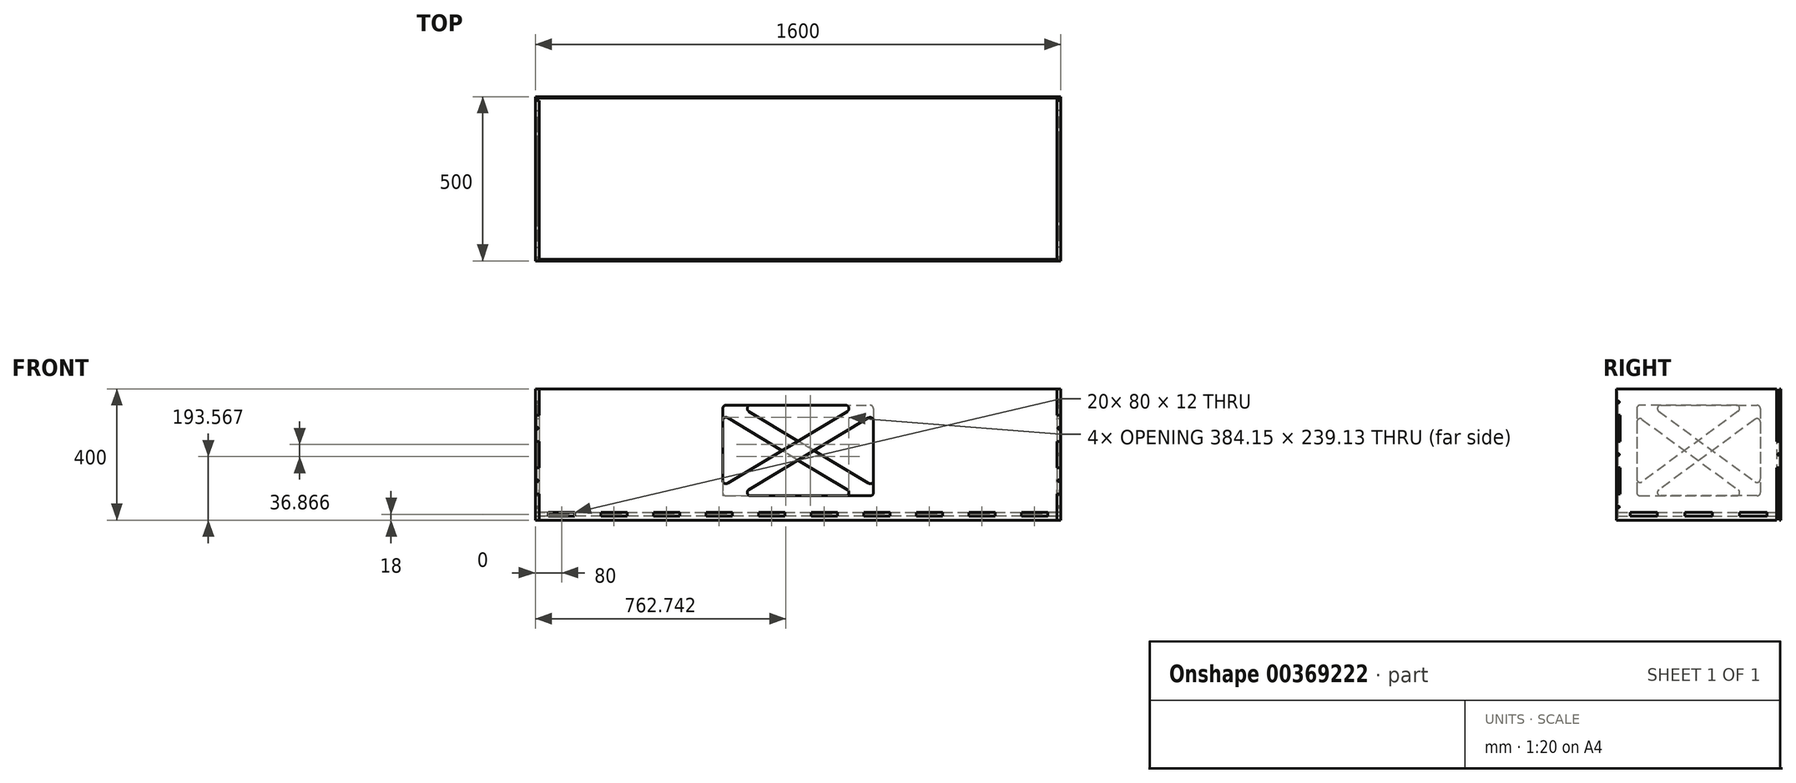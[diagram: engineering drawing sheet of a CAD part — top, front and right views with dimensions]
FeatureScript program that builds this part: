
annotation { "Feature Type Name" : "Feature", "Feature Type Description" : "" }
export const myFeature = defineFeature(function(context is Context, id is Id, definition is map)
    precondition{}
    {
        {
            assignVariable(context, id + "F0", {"name" : "lev", "anyValue" : 500});
        }
        {
            assignVariable(context, id + "F1", {"name" : "pit", "anyValue" : 1600});
        }
        {
            assignVariable(context, id + "F2", {"name" : "vaneri", "anyValue" : 12});
        }
        {
            assignVariable(context, id + "F3", {"name" : "ohut", "anyValue" : 4});
        }
        {
            var Q0;
            Q0=qCreatedBy(makeId("Right.planeOp"),FACE);
            var sketch = newSketch(context, id + "F4", { "sketchPlane" : qUnion([Q0])});
            skLineSegment(sketch, "E0.bottom", {"start": v(0, 0) * mm, "end": v(-500, 0) * mm});
            skLineSegment(sketch, "E0.top", {"start": v(0, 400) * mm, "end": v(-500, 400) * mm});
            skLineSegment(sketch, "E0.right", {"start": v(-500, 0) * mm, "end": v(-500, 80) * mm});
            skLineSegment(sketch, "E1.bottom", {"start": v(-500, 320) * mm, "end": v(-488, 320) * mm});
            skLineSegment(sketch, "E1.top", {"start": v(-500, 240) * mm, "end": v(-488, 240) * mm});
            skLineSegment(sketch, "E1.right", {"start": v(-488, 320) * mm, "end": v(-488, 240) * mm});
            skLineSegment(sketch, "E2.trimOffspring", {"start": v(-500, 320) * mm, "end": v(-500, 400) * mm});
            skCircle(sketch, "E3", {"center": v(-494, 360) * mm, "radius": 3 * mm});
            skPoint(sketch, "E3.centerSnap0", {"position": v(-500, 360) * mm});
            skPoint(sketch, "E3.centerSnap1", {"position": v(-494, 320) * mm});
            skLineSegment(sketch, "E4.bottom", {"start": v(-500, 160) * mm, "end": v(-488, 160) * mm});
            skLineSegment(sketch, "E4.top", {"start": v(-500, 80) * mm, "end": v(-488, 80) * mm});
            skLineSegment(sketch, "E4.right", {"start": v(-488, 160) * mm, "end": v(-488, 80) * mm});
            skLineSegment(sketch, "E5.trimOffspring", {"start": v(-500, 160) * mm, "end": v(-500, 240) * mm});
            skCircle(sketch, "E6", {"center": v(-494, 200) * mm, "radius": 3 * mm});
            skPoint(sketch, "E6.centerSnap0", {"position": v(-494, 240) * mm});
            skPoint(sketch, "E6.centerSnap1", {"position": v(-500, 200) * mm});
            skCircle(sketch, "E7", {"center": v(-494, 40) * mm, "radius": 3 * mm});
            skPoint(sketch, "E7.centerSnap0", {"position": v(-494, 80) * mm});
            skPoint(sketch, "E7.centerSnap1", {"position": v(-500, 40) * mm});
            skLineSegment(sketch, "E8", {"start": v(-250, 400) * mm, "end": v(-250, 0) * mm, "construction": true});
            skLineSegment(sketch, "E9.MirrorCS", {"start": v(0, 320) * mm, "end": v(0, 400) * mm});
            skLineSegment(sketch, "E10.MirrorCS", {"start": v(0, 0) * mm, "end": v(0, 80) * mm});
            skLineSegment(sketch, "E11.MirrorCS", {"start": v(0, 240) * mm, "end": v(-12, 240) * mm});
            skLineSegment(sketch, "E12.MirrorCS", {"start": v(0, 320) * mm, "end": v(-12, 320) * mm});
            skLineSegment(sketch, "E13.MirrorCS", {"start": v(0, 160) * mm, "end": v(-12, 160) * mm});
            skLineSegment(sketch, "E14.MirrorCS", {"start": v(0, 80) * mm, "end": v(-12, 80) * mm});
            skCircle(sketch, "E15.MirrorC", {"center": v(-6, 360) * mm, "radius": 3 * mm});
            skCircle(sketch, "E16.MirrorC", {"center": v(-6, 200) * mm, "radius": 3 * mm});
            skCircle(sketch, "E17.MirrorC", {"center": v(-6, 40) * mm, "radius": 3 * mm});
            skPoint(sketch, "E18.MirrorP", {"position": v(-6, 320) * mm});
            skLineSegment(sketch, "E19.MirrorCS", {"start": v(-12, 320) * mm, "end": v(-12, 240) * mm});
            skPoint(sketch, "E20.MirrorP", {"position": v(0, 40) * mm});
            skPoint(sketch, "E21.MirrorP", {"position": v(-6, 80) * mm});
            skPoint(sketch, "E22.MirrorP", {"position": v(0, 200) * mm});
            skLineSegment(sketch, "E23.MirrorCS", {"start": v(-12, 160) * mm, "end": v(-12, 80) * mm});
            skLineSegment(sketch, "E24.MirrorCS", {"start": v(0, 160) * mm, "end": v(0, 240) * mm});
            skPoint(sketch, "E25.MirrorP", {"position": v(0, 360) * mm});
            skPoint(sketch, "E26.MirrorP", {"position": v(-6, 240) * mm});
            skLineSegment(sketch, "E27.bottom", {"start": v(-458.33, 12) * mm, "end": v(-375, 12) * mm});
            skLineSegment(sketch, "E27.top", {"start": v(-458.33, 24) * mm, "end": v(-375, 24) * mm});
            skLineSegment(sketch, "E27.left", {"start": v(-458.33, 12) * mm, "end": v(-458.33, 24) * mm});
            skLineSegment(sketch, "E27.right", {"start": v(-375, 12) * mm, "end": v(-375, 24) * mm});
            skLineSegment(sketch, "E28.1.0.0", {"start": v(-208.33, 12) * mm, "end": v(-208.33, 24) * mm});
            skLineSegment(sketch, "E28.1.0.1", {"start": v(-291.67, 24) * mm, "end": v(-208.33, 24) * mm});
            skLineSegment(sketch, "E28.1.0.2", {"start": v(-291.67, 12) * mm, "end": v(-291.67, 24) * mm});
            skLineSegment(sketch, "E28.1.0.3", {"start": v(-291.67, 12) * mm, "end": v(-208.33, 12) * mm});
            skLineSegment(sketch, "E28.2.0.0", {"start": v(-41.67, 12) * mm, "end": v(-41.67, 24) * mm});
            skLineSegment(sketch, "E28.2.0.1", {"start": v(-125, 24) * mm, "end": v(-41.67, 24) * mm});
            skLineSegment(sketch, "E28.2.0.2", {"start": v(-125, 12) * mm, "end": v(-125, 24) * mm});
            skLineSegment(sketch, "E28.2.0.3", {"start": v(-125, 12) * mm, "end": v(-41.67, 12) * mm});
            skLineSegment(sketch, "E28.direction1", {"start": v(-458.33, 12) * mm, "end": v(-291.67, 12) * mm, "construction": true});
            skLineSegment(sketch, "E29.bottom", {"start": v(-365.23, 350) * mm, "end": v(-72, 350) * mm});
            skLineSegment(sketch, "E29.top", {"start": v(-428, 74) * mm, "end": v(-134.77, 74) * mm});
            skLineSegment(sketch, "E29.left", {"start": v(-438, 299.24) * mm, "end": v(-438, 84) * mm});
            skLineSegment(sketch, "E29.right", {"start": v(-62, 340) * mm, "end": v(-62, 124.76) * mm});
            skLineSegment(sketch, "E30", {"start": v(-438, 350) * mm, "end": v(-62, 74) * mm, "construction": true});
            skLineSegment(sketch, "E31", {"start": v(-371.15, 331.94) * mm, "end": v(-77.92, 116.7) * mm});
            skLineSegment(sketch, "E32", {"start": v(-422.08, 307.3) * mm, "end": v(-128.85, 92.06) * mm});
            skPoint(sketch, "E33.visualSharp", {"position": v(-438, 318.99) * mm});
            skArc(sketch, "E33.filletArc", {"start": v(-422.08, 307.3) * mm, "mid": v(-432.52, 308.16) * mm, "end": v(-438, 299.24) * mm});
            skPoint(sketch, "E34.visualSharp", {"position": v(-438, 74) * mm});
            skArc(sketch, "E34.filletArc", {"start": v(-438, 84) * mm, "mid": v(-435.07, 76.93) * mm, "end": v(-428, 74) * mm});
            skPoint(sketch, "E35.visualSharp", {"position": v(-104.25, 74) * mm});
            skArc(sketch, "E35.filletArc", {"start": v(-134.77, 74) * mm, "mid": v(-125.27, 80.89) * mm, "end": v(-128.85, 92.06) * mm});
            skPoint(sketch, "E36.visualSharp", {"position": v(-62, 105.01) * mm});
            skArc(sketch, "E36.filletArc", {"start": v(-77.92, 116.7) * mm, "mid": v(-67.48, 115.84) * mm, "end": v(-62, 124.76) * mm});
            skPoint(sketch, "E37.visualSharp", {"position": v(-395.75, 350) * mm});
            skArc(sketch, "E37.filletArc", {"start": v(-365.23, 350) * mm, "mid": v(-374.73, 343.11) * mm, "end": v(-371.15, 331.94) * mm});
            skPoint(sketch, "E38.visualSharp", {"position": v(-62, 350) * mm});
            skArc(sketch, "E38.filletArc", {"start": v(-62, 340) * mm, "mid": v(-64.93, 347.07) * mm, "end": v(-72, 350) * mm});
            skSolve(sketch);
        }
        {
            var Q0;
            Q0 = qSketchRegion(id + "F4", true);
            var Q1;
            Q1=makeQuery(id+"F4.imprint","IMPRINT",FACE,{"disambiguationData":[TD([[makeQuery(id+"F4.imprint","IMPRINT",EDGE,{"derivedFrom":sQuery(id+"F4.wireOp",EDGE,"E29.top")}),1.0]])]});
            var Q2;
            Q2=makeQuery(id+"F4.imprint","IMPRINT",FACE,{"disambiguationData":[TD([[makeQuery(id+"F4.imprint","IMPRINT",EDGE,{"derivedFrom":sQuery(id+"F4.wireOp",EDGE,"E29.bottom")}),-1.0]])]});
            extrude(context, id + "F5", {"entities" : qUnion([Q0, Q1, Q2]), "depth" : (getVariable(context, 'vaneri')) * mm});
        }
        {
            var Q0;
            Q0=makeQuery(id+"F4.imprint","IMPRINT",FACE,{"disambiguationData":[TD([[makeQuery(id+"F4.imprint","IMPRINT",EDGE,{"derivedFrom":sQuery(id+"F4.wireOp",EDGE,"E29.top")}),1.0]])]});
            var Q1;
            Q1=makeQuery(id+"F4.imprint","IMPRINT",FACE,{"disambiguationData":[TD([[makeQuery(id+"F4.imprint","IMPRINT",EDGE,{"derivedFrom":sQuery(id+"F4.wireOp",EDGE,"E29.bottom")}),-1.0]])]});
            extrude(context, id + "F6", {"entities" : qUnion([Q0, Q1]), "operationType" : NewBodyOperationType.REMOVE, "depth" : (getVariable(context, 'vaneri') - getVariable(context, 'ohut')) * mm});
        }
        {
            var Q0;
            Q0=makeQuery(id+"F5.opExtrude","SWEPT_BODY",BODY,{"disambiguationData":[OSD([sQuery(id+"F4.wireOp",EDGE,"E0.bottom"),sQuery(id+"F4.wireOp",EDGE,"E0.top"),sQuery(id+"F4.wireOp",EDGE,"E0.right"),sQuery(id+"F4.wireOp",EDGE,"E1.bottom"),sQuery(id+"F4.wireOp",EDGE,"E1.top"),sQuery(id+"F4.wireOp",EDGE,"E1.right"),sQuery(id+"F4.wireOp",EDGE,"E2.trimOffspring"),sQuery(id+"F4.wireOp",EDGE,"E3"),sQuery(id+"F4.wireOp",EDGE,"E4.bottom"),sQuery(id+"F4.wireOp",EDGE,"E4.top"),sQuery(id+"F4.wireOp",EDGE,"E4.right"),sQuery(id+"F4.wireOp",EDGE,"E5.trimOffspring"),sQuery(id+"F4.wireOp",EDGE,"E6"),sQuery(id+"F4.wireOp",EDGE,"E7"),sQuery(id+"F4.wireOp",EDGE,"E9.MirrorCS"),sQuery(id+"F4.wireOp",EDGE,"E10.MirrorCS"),sQuery(id+"F4.wireOp",EDGE,"E11.MirrorCS"),sQuery(id+"F4.wireOp",EDGE,"E12.MirrorCS"),sQuery(id+"F4.wireOp",EDGE,"E13.MirrorCS"),sQuery(id+"F4.wireOp",EDGE,"E14.MirrorCS"),sQuery(id+"F4.wireOp",EDGE,"E15.MirrorC"),sQuery(id+"F4.wireOp",EDGE,"E16.MirrorC"),sQuery(id+"F4.wireOp",EDGE,"E17.MirrorC"),sQuery(id+"F4.wireOp",EDGE,"E19.MirrorCS"),sQuery(id+"F4.wireOp",EDGE,"E23.MirrorCS"),sQuery(id+"F4.wireOp",EDGE,"E24.MirrorCS"),sQuery(id+"F4.wireOp",EDGE,"E27.bottom"),sQuery(id+"F4.wireOp",EDGE,"E27.top"),sQuery(id+"F4.wireOp",EDGE,"E27.left"),sQuery(id+"F4.wireOp",EDGE,"E27.right"),sQuery(id+"F4.wireOp",EDGE,"E28.1.0.0"),sQuery(id+"F4.wireOp",EDGE,"E28.1.0.1"),sQuery(id+"F4.wireOp",EDGE,"E28.1.0.2"),sQuery(id+"F4.wireOp",EDGE,"E28.1.0.3"),sQuery(id+"F4.wireOp",EDGE,"E28.2.0.0"),sQuery(id+"F4.wireOp",EDGE,"E28.2.0.1"),sQuery(id+"F4.wireOp",EDGE,"E28.2.0.2"),sQuery(id+"F4.wireOp",EDGE,"E28.2.0.3")])]});
            var Q1;
            Q1=sQuery(id+"F4.wireOp",EDGE,"E8");
            transform(context, id + "F7", {"entities" : qUnion([Q0]), "transformType" : TransformType.ROTATION, "transformAxis" : qUnion([Q1]), "angle" : 180 * degree, "makeCopy" : true});
        }
        {
            var Q0;
            Q0=makeQuery(id+"F7.opPattern","COPY",BODY,{"derivedFrom":makeQuery(id+"F5.opExtrude","SWEPT_BODY",BODY,{"disambiguationData":[OSD([sQuery(id+"F4.wireOp",EDGE,"E0.bottom"),sQuery(id+"F4.wireOp",EDGE,"E0.top"),sQuery(id+"F4.wireOp",EDGE,"E0.right"),sQuery(id+"F4.wireOp",EDGE,"E1.bottom"),sQuery(id+"F4.wireOp",EDGE,"E1.top"),sQuery(id+"F4.wireOp",EDGE,"E1.right"),sQuery(id+"F4.wireOp",EDGE,"E2.trimOffspring"),sQuery(id+"F4.wireOp",EDGE,"E3"),sQuery(id+"F4.wireOp",EDGE,"E4.bottom"),sQuery(id+"F4.wireOp",EDGE,"E4.top"),sQuery(id+"F4.wireOp",EDGE,"E4.right"),sQuery(id+"F4.wireOp",EDGE,"E5.trimOffspring"),sQuery(id+"F4.wireOp",EDGE,"E6"),sQuery(id+"F4.wireOp",EDGE,"E7"),sQuery(id+"F4.wireOp",EDGE,"E9.MirrorCS"),sQuery(id+"F4.wireOp",EDGE,"E10.MirrorCS"),sQuery(id+"F4.wireOp",EDGE,"E11.MirrorCS"),sQuery(id+"F4.wireOp",EDGE,"E12.MirrorCS"),sQuery(id+"F4.wireOp",EDGE,"E13.MirrorCS"),sQuery(id+"F4.wireOp",EDGE,"E14.MirrorCS"),sQuery(id+"F4.wireOp",EDGE,"E15.MirrorC"),sQuery(id+"F4.wireOp",EDGE,"E16.MirrorC"),sQuery(id+"F4.wireOp",EDGE,"E17.MirrorC"),sQuery(id+"F4.wireOp",EDGE,"E19.MirrorCS"),sQuery(id+"F4.wireOp",EDGE,"E23.MirrorCS"),sQuery(id+"F4.wireOp",EDGE,"E24.MirrorCS"),sQuery(id+"F4.wireOp",EDGE,"E27.bottom"),sQuery(id+"F4.wireOp",EDGE,"E27.top"),sQuery(id+"F4.wireOp",EDGE,"E27.left"),sQuery(id+"F4.wireOp",EDGE,"E27.right"),sQuery(id+"F4.wireOp",EDGE,"E28.1.0.0"),sQuery(id+"F4.wireOp",EDGE,"E28.1.0.1"),sQuery(id+"F4.wireOp",EDGE,"E28.1.0.2"),sQuery(id+"F4.wireOp",EDGE,"E28.1.0.3"),sQuery(id+"F4.wireOp",EDGE,"E28.2.0.0"),sQuery(id+"F4.wireOp",EDGE,"E28.2.0.1"),sQuery(id+"F4.wireOp",EDGE,"E28.2.0.2"),sQuery(id+"F4.wireOp",EDGE,"E28.2.0.3")])]}),"instanceName":"1"});
            transform(context, id + "F8", {"entities" : qUnion([Q0]), "transformType" : TransformType.TRANSLATION_3D, "dx" : (-(getVariable(context, 'pit') - 2 * getVariable(context, 'vaneri'))) * mm, "dy" : 0 * mm, "dz" : 0 * mm, "makeCopy" : false});
        }
        {
            var Q0;
            Q0=makeQuery(id+"F5.opExtrude","SWEPT_FACE",FACE,{"disambiguationData":[OSD([sQuery(id+"F4.wireOp",EDGE,"E24.MirrorCS")])]});
            var sketch = newSketch(context, id + "F9", { "sketchPlane" : qUnion([Q0])});
            skLineSegment(sketch, "E39.bottom", {"start": v(-12, 400) * mm, "end": v(1588, 400) * mm});
            skLineSegment(sketch, "E39.top", {"start": v(-12, 0) * mm, "end": v(1588, 0) * mm});
            skLineSegment(sketch, "E39.left", {"start": v(-12, 400) * mm, "end": v(-12, 0) * mm});
            skLineSegment(sketch, "E39.right", {"start": v(1588, 400) * mm, "end": v(1588, 0) * mm});
            skLineSegment(sketch, "E40.bottom", {"start": v(28, 12) * mm, "end": v(108, 12) * mm});
            skLineSegment(sketch, "E40.top", {"start": v(28, 24) * mm, "end": v(108, 24) * mm});
            skLineSegment(sketch, "E40.left", {"start": v(28, 12) * mm, "end": v(28, 24) * mm});
            skLineSegment(sketch, "E40.right", {"start": v(108, 12) * mm, "end": v(108, 24) * mm});
            skLineSegment(sketch, "E41.1.0.0", {"start": v(188, 24) * mm, "end": v(268, 24) * mm});
            skLineSegment(sketch, "E41.1.0.1", {"start": v(268, 12) * mm, "end": v(268, 24) * mm});
            skLineSegment(sketch, "E41.1.0.2", {"start": v(188, 12) * mm, "end": v(268, 12) * mm});
            skLineSegment(sketch, "E41.1.0.3", {"start": v(188, 12) * mm, "end": v(188, 24) * mm});
            skLineSegment(sketch, "E41.2.0.0", {"start": v(348, 24) * mm, "end": v(428, 24) * mm});
            skLineSegment(sketch, "E41.2.0.1", {"start": v(428, 12) * mm, "end": v(428, 24) * mm});
            skLineSegment(sketch, "E41.2.0.2", {"start": v(348, 12) * mm, "end": v(428, 12) * mm});
            skLineSegment(sketch, "E41.2.0.3", {"start": v(348, 12) * mm, "end": v(348, 24) * mm});
            skLineSegment(sketch, "E41.3.0.0", {"start": v(508, 24) * mm, "end": v(588, 24) * mm});
            skLineSegment(sketch, "E41.3.0.1", {"start": v(588, 12) * mm, "end": v(588, 24) * mm});
            skLineSegment(sketch, "E41.3.0.2", {"start": v(508, 12) * mm, "end": v(588, 12) * mm});
            skLineSegment(sketch, "E41.3.0.3", {"start": v(508, 12) * mm, "end": v(508, 24) * mm});
            skLineSegment(sketch, "E41.4.0.0", {"start": v(668, 24) * mm, "end": v(748, 24) * mm});
            skLineSegment(sketch, "E41.4.0.1", {"start": v(748, 12) * mm, "end": v(748, 24) * mm});
            skLineSegment(sketch, "E41.4.0.2", {"start": v(668, 12) * mm, "end": v(748, 12) * mm});
            skLineSegment(sketch, "E41.4.0.3", {"start": v(668, 12) * mm, "end": v(668, 24) * mm});
            skLineSegment(sketch, "E41.5.0.0", {"start": v(828, 24) * mm, "end": v(908, 24) * mm});
            skLineSegment(sketch, "E41.5.0.1", {"start": v(908, 12) * mm, "end": v(908, 24) * mm});
            skLineSegment(sketch, "E41.5.0.2", {"start": v(828, 12) * mm, "end": v(908, 12) * mm});
            skLineSegment(sketch, "E41.5.0.3", {"start": v(828, 12) * mm, "end": v(828, 24) * mm});
            skLineSegment(sketch, "E41.6.0.0", {"start": v(988, 24) * mm, "end": v(1068, 24) * mm});
            skLineSegment(sketch, "E41.6.0.1", {"start": v(1068, 12) * mm, "end": v(1068, 24) * mm});
            skLineSegment(sketch, "E41.6.0.2", {"start": v(988, 12) * mm, "end": v(1068, 12) * mm});
            skLineSegment(sketch, "E41.6.0.3", {"start": v(988, 12) * mm, "end": v(988, 24) * mm});
            skLineSegment(sketch, "E41.7.0.0", {"start": v(1148, 24) * mm, "end": v(1228, 24) * mm});
            skLineSegment(sketch, "E41.7.0.1", {"start": v(1228, 12) * mm, "end": v(1228, 24) * mm});
            skLineSegment(sketch, "E41.7.0.2", {"start": v(1148, 12) * mm, "end": v(1228, 12) * mm});
            skLineSegment(sketch, "E41.7.0.3", {"start": v(1148, 12) * mm, "end": v(1148, 24) * mm});
            skLineSegment(sketch, "E41.8.0.0", {"start": v(1308, 24) * mm, "end": v(1388, 24) * mm});
            skLineSegment(sketch, "E41.8.0.1", {"start": v(1388, 12) * mm, "end": v(1388, 24) * mm});
            skLineSegment(sketch, "E41.8.0.2", {"start": v(1308, 12) * mm, "end": v(1388, 12) * mm});
            skLineSegment(sketch, "E41.8.0.3", {"start": v(1308, 12) * mm, "end": v(1308, 24) * mm});
            skLineSegment(sketch, "E41.9.0.0", {"start": v(1468, 24) * mm, "end": v(1548, 24) * mm});
            skLineSegment(sketch, "E41.9.0.1", {"start": v(1548, 12) * mm, "end": v(1548, 24) * mm});
            skLineSegment(sketch, "E41.9.0.2", {"start": v(1468, 12) * mm, "end": v(1548, 12) * mm});
            skLineSegment(sketch, "E41.9.0.3", {"start": v(1468, 12) * mm, "end": v(1468, 24) * mm});
            skLineSegment(sketch, "E41.direction1", {"start": v(28, 12) * mm, "end": v(188, 12) * mm, "construction": true});
            skLineSegment(sketch, "E42", {"start": v(50, 303.13) * mm, "end": v(50, 84) * mm});
            skLineSegment(sketch, "E43", {"start": v(60, 74) * mm, "end": v(424.17, 74) * mm});
            skLineSegment(sketch, "E44", {"start": v(429.32, 92.57) * mm, "end": v(65.16, 311.7) * mm});
            skLineSegment(sketch, "E45", {"start": v(134.5, 350) * mm, "end": v(498.67, 350) * mm});
            skLineSegment(sketch, "E46", {"start": v(508.67, 340) * mm, "end": v(508.67, 120.87) * mm});
            skLineSegment(sketch, "E47", {"start": v(493.51, 112.3) * mm, "end": v(129.35, 331.43) * mm});
            skLineSegment(sketch, "E48", {"start": v(508.67, 103.18) * mm, "end": v(508.67, 74) * mm, "construction": true});
            skLineSegment(sketch, "E49", {"start": v(508.67, 74) * mm, "end": v(460.18, 74) * mm, "construction": true});
            skLineSegment(sketch, "E50", {"start": v(50, 320.82) * mm, "end": v(50, 350) * mm, "construction": true});
            skLineSegment(sketch, "E51", {"start": v(50, 350) * mm, "end": v(98.49, 350) * mm, "construction": true});
            skLineSegment(sketch, "E52", {"start": v(50, 350) * mm, "end": v(508.67, 74) * mm, "construction": true});
            skLineSegment(sketch, "E53", {"start": v(533.67, 400) * mm, "end": v(533.67, 0) * mm, "construction": true});
            skArc(sketch, "E54", {"start": v(50, 84) * mm, "mid": v(52.93, 76.93) * mm, "end": v(60, 74) * mm});
            skArc(sketch, "E55", {"start": v(65.16, 311.7) * mm, "mid": v(55.08, 311.84) * mm, "end": v(50, 303.13) * mm});
            skArc(sketch, "E56", {"start": v(424.17, 74) * mm, "mid": v(433.8, 81.32) * mm, "end": v(429.32, 92.57) * mm});
            skArc(sketch, "E57", {"start": v(134.5, 350) * mm, "mid": v(124.87, 342.68) * mm, "end": v(129.35, 331.43) * mm});
            skArc(sketch, "E58", {"start": v(508.67, 340) * mm, "mid": v(505.74, 347.07) * mm, "end": v(498.67, 350) * mm});
            skArc(sketch, "E59", {"start": v(493.51, 112.3) * mm, "mid": v(503.59, 112.16) * mm, "end": v(508.67, 120.87) * mm});
            skArc(sketch, "E60.MirrorCS", {"start": v(573.82, 112.3) * mm, "mid": v(563.75, 112.16) * mm, "end": v(558.67, 120.87) * mm});
            skArc(sketch, "E61.MirrorCS", {"start": v(932.83, 350) * mm, "mid": v(942.47, 342.68) * mm, "end": v(937.99, 331.43) * mm});
            skArc(sketch, "E62.MirrorCS", {"start": v(558.67, 340) * mm, "mid": v(561.6, 347.07) * mm, "end": v(568.67, 350) * mm});
            skArc(sketch, "E63.MirrorCS", {"start": v(1017.33, 84) * mm, "mid": v(1014.4, 76.93) * mm, "end": v(1007.33, 74) * mm});
            skArc(sketch, "E64.MirrorCS", {"start": v(1002.18, 311.7) * mm, "mid": v(1012.25, 311.84) * mm, "end": v(1017.33, 303.13) * mm});
            skLineSegment(sketch, "E65.MirrorCS", {"start": v(1017.33, 350) * mm, "end": v(558.67, 74) * mm, "construction": true});
            skLineSegment(sketch, "E66.MirrorCS", {"start": v(932.83, 350) * mm, "end": v(568.67, 350) * mm});
            skLineSegment(sketch, "E67.MirrorCS", {"start": v(1017.33, 320.82) * mm, "end": v(1017.33, 350) * mm, "construction": true});
            skLineSegment(sketch, "E68.MirrorCS", {"start": v(638.01, 92.57) * mm, "end": v(1002.18, 311.7) * mm});
            skLineSegment(sketch, "E69.MirrorCS", {"start": v(1017.33, 350) * mm, "end": v(968.85, 350) * mm, "construction": true});
            skArc(sketch, "E70.MirrorCS", {"start": v(643.17, 74) * mm, "mid": v(633.53, 81.32) * mm, "end": v(638.01, 92.57) * mm});
            skLineSegment(sketch, "E71.MirrorCS", {"start": v(1007.33, 74) * mm, "end": v(643.17, 74) * mm});
            skLineSegment(sketch, "E72.MirrorCS", {"start": v(558.67, 74) * mm, "end": v(607.15, 74) * mm, "construction": true});
            skLineSegment(sketch, "E73.MirrorCS", {"start": v(558.67, 103.18) * mm, "end": v(558.67, 74) * mm, "construction": true});
            skLineSegment(sketch, "E74.MirrorCS", {"start": v(1017.33, 303.13) * mm, "end": v(1017.33, 84) * mm});
            skLineSegment(sketch, "E75.MirrorCS", {"start": v(558.67, 340) * mm, "end": v(558.67, 120.87) * mm});
            skLineSegment(sketch, "E76.MirrorCS", {"start": v(573.82, 112.3) * mm, "end": v(937.99, 331.43) * mm});
            skLineSegment(sketch, "E77", {"start": v(1042.33, 400) * mm, "end": v(1042.33, 0) * mm, "construction": true});
            skArc(sketch, "E78.MirrorCS", {"start": v(1151.83, 350) * mm, "mid": v(1142.2, 342.68) * mm, "end": v(1146.68, 331.43) * mm});
            skArc(sketch, "E79.MirrorCS", {"start": v(1082.49, 311.7) * mm, "mid": v(1072.41, 311.84) * mm, "end": v(1067.33, 303.13) * mm});
            skArc(sketch, "E80.MirrorCS", {"start": v(1526, 340) * mm, "mid": v(1523.07, 347.07) * mm, "end": v(1516, 350) * mm});
            skArc(sketch, "E81.MirrorCS", {"start": v(1441.5, 74) * mm, "mid": v(1451.13, 81.32) * mm, "end": v(1446.65, 92.57) * mm});
            skArc(sketch, "E82.MirrorCS", {"start": v(1510.84, 112.3) * mm, "mid": v(1520.92, 112.16) * mm, "end": v(1526, 120.87) * mm});
            skArc(sketch, "E83.MirrorCS", {"start": v(1067.33, 84) * mm, "mid": v(1070.26, 76.93) * mm, "end": v(1077.33, 74) * mm});
            skLineSegment(sketch, "E84.MirrorCS", {"start": v(1526, 103.18) * mm, "end": v(1526, 74) * mm, "construction": true});
            skLineSegment(sketch, "E85.MirrorCS", {"start": v(1151.83, 350) * mm, "end": v(1516, 350) * mm});
            skLineSegment(sketch, "E86.MirrorCS", {"start": v(1077.33, 74) * mm, "end": v(1441.5, 74) * mm});
            skLineSegment(sketch, "E87.MirrorCS", {"start": v(1446.65, 92.57) * mm, "end": v(1082.49, 311.7) * mm});
            skLineSegment(sketch, "E88.MirrorCS", {"start": v(1526, 340) * mm, "end": v(1526, 120.87) * mm});
            skLineSegment(sketch, "E89.MirrorCS", {"start": v(1510.84, 112.3) * mm, "end": v(1146.68, 331.43) * mm});
            skLineSegment(sketch, "E90.MirrorCS", {"start": v(1067.33, 320.82) * mm, "end": v(1067.33, 350) * mm, "construction": true});
            skLineSegment(sketch, "E91.MirrorCS", {"start": v(1526, 74) * mm, "end": v(1477.51, 74) * mm, "construction": true});
            skLineSegment(sketch, "E92.MirrorCS", {"start": v(1067.33, 350) * mm, "end": v(1115.82, 350) * mm, "construction": true});
            skLineSegment(sketch, "E93.MirrorCS", {"start": v(1067.33, 350) * mm, "end": v(1526, 74) * mm, "construction": true});
            skLineSegment(sketch, "E94.MirrorCS", {"start": v(1067.33, 303.13) * mm, "end": v(1067.33, 84) * mm});
            skCircle(sketch, "E95", {"center": v(-6, 280) * mm, "radius": 3 * mm});
            skCircle(sketch, "E96", {"center": v(-6, 120) * mm, "radius": 3 * mm});
            skLineSegment(sketch, "E97", {"start": v(-12, 280) * mm, "end": v(0, 280) * mm, "construction": true});
            skLineSegment(sketch, "E98", {"start": v(-12, 120) * mm, "end": v(0, 120) * mm, "construction": true});
            skLineSegment(sketch, "E99", {"start": v(788, 400) * mm, "end": v(788, 0) * mm, "construction": true});
            skCircle(sketch, "E100.MirrorC", {"center": v(1582, 280) * mm, "radius": 3 * mm});
            skCircle(sketch, "E101.MirrorC", {"center": v(1582, 120) * mm, "radius": 3 * mm});
            skLineSegment(sketch, "E102.MirrorCS", {"start": v(1588, 280) * mm, "end": v(1576, 280) * mm, "construction": true});
            skLineSegment(sketch, "E103.MirrorCS", {"start": v(1588, 120) * mm, "end": v(1576, 120) * mm, "construction": true});
            skSolve(sketch);
        }
        {
            var Q0;
            Q0 = qSketchRegion(id + "F9", true);
            var Q1;
            Q1=makeQuery(id+"F9.imprint","IMPRINT",FACE,{"disambiguationData":[TD([[makeQuery(id+"F9.imprint","IMPRINT",EDGE,{"derivedFrom":sQuery(id+"F9.wireOp",EDGE,"E42")}),1.0]])]});
            var Q2;
            Q2=makeQuery(id+"F9.imprint","IMPRINT",FACE,{"disambiguationData":[TD([[makeQuery(id+"F9.imprint","IMPRINT",EDGE,{"derivedFrom":sQuery(id+"F9.wireOp",EDGE,"E45")}),-1.0]])]});
            var Q3;
            Q3=makeQuery(id+"F9.imprint","IMPRINT",FACE,{"disambiguationData":[TD([[makeQuery(id+"F9.imprint","IMPRINT",EDGE,{"derivedFrom":sQuery(id+"F9.wireOp",EDGE,"E60.MirrorCS")}),-1.0]])]});
            var Q4;
            Q4=makeQuery(id+"F9.imprint","IMPRINT",FACE,{"disambiguationData":[TD([[makeQuery(id+"F9.imprint","IMPRINT",EDGE,{"derivedFrom":sQuery(id+"F9.wireOp",EDGE,"E63.MirrorCS")}),-1.0]])]});
            var Q5;
            Q5=makeQuery(id+"F9.imprint","IMPRINT",FACE,{"disambiguationData":[TD([[makeQuery(id+"F9.imprint","IMPRINT",EDGE,{"derivedFrom":sQuery(id+"F9.wireOp",EDGE,"E79.MirrorCS")}),1.0]])]});
            var Q6;
            Q6=makeQuery(id+"F9.imprint","IMPRINT",FACE,{"disambiguationData":[TD([[makeQuery(id+"F9.imprint","IMPRINT",EDGE,{"derivedFrom":sQuery(id+"F9.wireOp",EDGE,"E78.MirrorCS")}),1.0]])]});
            extrude(context, id + "F10", {"entities" : qUnion([Q0, Q1, Q2, Q3, Q4, Q5, Q6]), "oppositeDirection" : true, "depth" : (getVariable(context, 'vaneri')) * mm});
        }
        {
            var Q0;
            Q0=makeQuery(id+"F9.imprint","IMPRINT",FACE,{"disambiguationData":[TD([[makeQuery(id+"F9.imprint","IMPRINT",EDGE,{"derivedFrom":sQuery(id+"F9.wireOp",EDGE,"E42")}),1.0]])]});
            var Q1;
            Q1=makeQuery(id+"F9.imprint","IMPRINT",FACE,{"disambiguationData":[TD([[makeQuery(id+"F9.imprint","IMPRINT",EDGE,{"derivedFrom":sQuery(id+"F9.wireOp",EDGE,"E45")}),-1.0]])]});
            var Q2;
            Q2=makeQuery(id+"F9.imprint","IMPRINT",FACE,{"disambiguationData":[TD([[makeQuery(id+"F9.imprint","IMPRINT",EDGE,{"derivedFrom":sQuery(id+"F9.wireOp",EDGE,"E60.MirrorCS")}),-1.0]])]});
            var Q3;
            Q3=makeQuery(id+"F9.imprint","IMPRINT",FACE,{"disambiguationData":[TD([[makeQuery(id+"F9.imprint","IMPRINT",EDGE,{"derivedFrom":sQuery(id+"F9.wireOp",EDGE,"E63.MirrorCS")}),-1.0]])]});
            var Q4;
            Q4=makeQuery(id+"F9.imprint","IMPRINT",FACE,{"disambiguationData":[TD([[makeQuery(id+"F9.imprint","IMPRINT",EDGE,{"derivedFrom":sQuery(id+"F9.wireOp",EDGE,"E79.MirrorCS")}),1.0]])]});
            var Q5;
            Q5=makeQuery(id+"F9.imprint","IMPRINT",FACE,{"disambiguationData":[TD([[makeQuery(id+"F9.imprint","IMPRINT",EDGE,{"derivedFrom":sQuery(id+"F9.wireOp",EDGE,"E78.MirrorCS")}),1.0]])]});
            extrude(context, id + "F11", {"entities" : qUnion([Q0, Q1, Q2, Q3, Q4, Q5]), "operationType" : NewBodyOperationType.REMOVE, "oppositeDirection" : true, "depth" : (getVariable(context, 'vaneri')) * mm, "hasSecondDirection" : true, "secondDirectionOppositeDirection" : true, "secondDirectionDepth" : (getVariable(context, 'ohut')) * mm});
        }
        {
            var Q0;
            Q0=makeQuery(id+"F5.opExtrude","SWEPT_BODY",BODY,{"disambiguationData":[OSD([sQuery(id+"F4.wireOp",EDGE,"E0.bottom"),sQuery(id+"F4.wireOp",EDGE,"E0.top"),sQuery(id+"F4.wireOp",EDGE,"E0.right"),sQuery(id+"F4.wireOp",EDGE,"E1.bottom"),sQuery(id+"F4.wireOp",EDGE,"E1.top"),sQuery(id+"F4.wireOp",EDGE,"E1.right"),sQuery(id+"F4.wireOp",EDGE,"E2.trimOffspring"),sQuery(id+"F4.wireOp",EDGE,"E3"),sQuery(id+"F4.wireOp",EDGE,"E4.bottom"),sQuery(id+"F4.wireOp",EDGE,"E4.top"),sQuery(id+"F4.wireOp",EDGE,"E4.right"),sQuery(id+"F4.wireOp",EDGE,"E5.trimOffspring"),sQuery(id+"F4.wireOp",EDGE,"E6"),sQuery(id+"F4.wireOp",EDGE,"E7"),sQuery(id+"F4.wireOp",EDGE,"E9.MirrorCS"),sQuery(id+"F4.wireOp",EDGE,"E10.MirrorCS"),sQuery(id+"F4.wireOp",EDGE,"E11.MirrorCS"),sQuery(id+"F4.wireOp",EDGE,"E12.MirrorCS"),sQuery(id+"F4.wireOp",EDGE,"E13.MirrorCS"),sQuery(id+"F4.wireOp",EDGE,"E14.MirrorCS"),sQuery(id+"F4.wireOp",EDGE,"E15.MirrorC"),sQuery(id+"F4.wireOp",EDGE,"E16.MirrorC"),sQuery(id+"F4.wireOp",EDGE,"E17.MirrorC"),sQuery(id+"F4.wireOp",EDGE,"E19.MirrorCS"),sQuery(id+"F4.wireOp",EDGE,"E23.MirrorCS"),sQuery(id+"F4.wireOp",EDGE,"E24.MirrorCS"),sQuery(id+"F4.wireOp",EDGE,"E27.bottom"),sQuery(id+"F4.wireOp",EDGE,"E27.top"),sQuery(id+"F4.wireOp",EDGE,"E27.left"),sQuery(id+"F4.wireOp",EDGE,"E27.right"),sQuery(id+"F4.wireOp",EDGE,"E28.1.0.0"),sQuery(id+"F4.wireOp",EDGE,"E28.1.0.1"),sQuery(id+"F4.wireOp",EDGE,"E28.1.0.2"),sQuery(id+"F4.wireOp",EDGE,"E28.1.0.3"),sQuery(id+"F4.wireOp",EDGE,"E28.2.0.0"),sQuery(id+"F4.wireOp",EDGE,"E28.2.0.1"),sQuery(id+"F4.wireOp",EDGE,"E28.2.0.2"),sQuery(id+"F4.wireOp",EDGE,"E28.2.0.3")])]});
            var Q1;
            Q1=makeQuery(id+"F7.opPattern","COPY",BODY,{"derivedFrom":makeQuery(id+"F5.opExtrude","SWEPT_BODY",BODY,{"disambiguationData":[OSD([sQuery(id+"F4.wireOp",EDGE,"E0.bottom"),sQuery(id+"F4.wireOp",EDGE,"E0.top"),sQuery(id+"F4.wireOp",EDGE,"E0.right"),sQuery(id+"F4.wireOp",EDGE,"E1.bottom"),sQuery(id+"F4.wireOp",EDGE,"E1.top"),sQuery(id+"F4.wireOp",EDGE,"E1.right"),sQuery(id+"F4.wireOp",EDGE,"E2.trimOffspring"),sQuery(id+"F4.wireOp",EDGE,"E3"),sQuery(id+"F4.wireOp",EDGE,"E4.bottom"),sQuery(id+"F4.wireOp",EDGE,"E4.top"),sQuery(id+"F4.wireOp",EDGE,"E4.right"),sQuery(id+"F4.wireOp",EDGE,"E5.trimOffspring"),sQuery(id+"F4.wireOp",EDGE,"E6"),sQuery(id+"F4.wireOp",EDGE,"E7"),sQuery(id+"F4.wireOp",EDGE,"E9.MirrorCS"),sQuery(id+"F4.wireOp",EDGE,"E10.MirrorCS"),sQuery(id+"F4.wireOp",EDGE,"E11.MirrorCS"),sQuery(id+"F4.wireOp",EDGE,"E12.MirrorCS"),sQuery(id+"F4.wireOp",EDGE,"E13.MirrorCS"),sQuery(id+"F4.wireOp",EDGE,"E14.MirrorCS"),sQuery(id+"F4.wireOp",EDGE,"E15.MirrorC"),sQuery(id+"F4.wireOp",EDGE,"E16.MirrorC"),sQuery(id+"F4.wireOp",EDGE,"E17.MirrorC"),sQuery(id+"F4.wireOp",EDGE,"E19.MirrorCS"),sQuery(id+"F4.wireOp",EDGE,"E23.MirrorCS"),sQuery(id+"F4.wireOp",EDGE,"E24.MirrorCS"),sQuery(id+"F4.wireOp",EDGE,"E27.bottom"),sQuery(id+"F4.wireOp",EDGE,"E27.top"),sQuery(id+"F4.wireOp",EDGE,"E27.left"),sQuery(id+"F4.wireOp",EDGE,"E27.right"),sQuery(id+"F4.wireOp",EDGE,"E28.1.0.0"),sQuery(id+"F4.wireOp",EDGE,"E28.1.0.1"),sQuery(id+"F4.wireOp",EDGE,"E28.1.0.2"),sQuery(id+"F4.wireOp",EDGE,"E28.1.0.3"),sQuery(id+"F4.wireOp",EDGE,"E28.2.0.0"),sQuery(id+"F4.wireOp",EDGE,"E28.2.0.1"),sQuery(id+"F4.wireOp",EDGE,"E28.2.0.2"),sQuery(id+"F4.wireOp",EDGE,"E28.2.0.3")])]}),"instanceName":"1"});
            var Q2;
            Q2=makeQuery(id+"F10.opExtrude","SWEPT_BODY",BODY,{"disambiguationData":[OSD([sQuery(id+"F9.wireOp",EDGE,"E39.bottom"),sQuery(id+"F9.wireOp",EDGE,"E39.top"),sQuery(id+"F9.wireOp",EDGE,"E39.left"),sQuery(id+"F9.wireOp",EDGE,"E39.right"),sQuery(id+"F9.wireOp",EDGE,"E40.bottom"),sQuery(id+"F9.wireOp",EDGE,"E40.top"),sQuery(id+"F9.wireOp",EDGE,"E40.left"),sQuery(id+"F9.wireOp",EDGE,"E40.right"),sQuery(id+"F9.wireOp",EDGE,"E41.1.0.0"),sQuery(id+"F9.wireOp",EDGE,"E41.1.0.1"),sQuery(id+"F9.wireOp",EDGE,"E41.1.0.2"),sQuery(id+"F9.wireOp",EDGE,"E41.1.0.3"),sQuery(id+"F9.wireOp",EDGE,"E41.2.0.0"),sQuery(id+"F9.wireOp",EDGE,"E41.2.0.1"),sQuery(id+"F9.wireOp",EDGE,"E41.2.0.2"),sQuery(id+"F9.wireOp",EDGE,"E41.2.0.3"),sQuery(id+"F9.wireOp",EDGE,"E41.3.0.0"),sQuery(id+"F9.wireOp",EDGE,"E41.3.0.1"),sQuery(id+"F9.wireOp",EDGE,"E41.3.0.2"),sQuery(id+"F9.wireOp",EDGE,"E41.3.0.3"),sQuery(id+"F9.wireOp",EDGE,"E41.4.0.0"),sQuery(id+"F9.wireOp",EDGE,"E41.4.0.1"),sQuery(id+"F9.wireOp",EDGE,"E41.4.0.2"),sQuery(id+"F9.wireOp",EDGE,"E41.4.0.3"),sQuery(id+"F9.wireOp",EDGE,"E41.5.0.0"),sQuery(id+"F9.wireOp",EDGE,"E41.5.0.1"),sQuery(id+"F9.wireOp",EDGE,"E41.5.0.2"),sQuery(id+"F9.wireOp",EDGE,"E41.5.0.3"),sQuery(id+"F9.wireOp",EDGE,"E41.6.0.0"),sQuery(id+"F9.wireOp",EDGE,"E41.6.0.1"),sQuery(id+"F9.wireOp",EDGE,"E41.6.0.2"),sQuery(id+"F9.wireOp",EDGE,"E41.6.0.3"),sQuery(id+"F9.wireOp",EDGE,"E41.7.0.0"),sQuery(id+"F9.wireOp",EDGE,"E41.7.0.1"),sQuery(id+"F9.wireOp",EDGE,"E41.7.0.2"),sQuery(id+"F9.wireOp",EDGE,"E41.7.0.3"),sQuery(id+"F9.wireOp",EDGE,"E41.8.0.0"),sQuery(id+"F9.wireOp",EDGE,"E41.8.0.1"),sQuery(id+"F9.wireOp",EDGE,"E41.8.0.2"),sQuery(id+"F9.wireOp",EDGE,"E41.8.0.3"),sQuery(id+"F9.wireOp",EDGE,"E41.9.0.0"),sQuery(id+"F9.wireOp",EDGE,"E41.9.0.1"),sQuery(id+"F9.wireOp",EDGE,"E41.9.0.2"),sQuery(id+"F9.wireOp",EDGE,"E41.9.0.3"),sQuery(id+"F9.wireOp",EDGE,"E95"),sQuery(id+"F9.wireOp",EDGE,"E96"),sQuery(id+"F9.wireOp",EDGE,"E100.MirrorC"),sQuery(id+"F9.wireOp",EDGE,"E101.MirrorC")])]});
            booleanBodies(context, id + "F12", {"operationType" : BooleanOperationType.SUBTRACTION, "tools" : qUnion([Q0, Q1]), "targets" : qUnion([Q2]), "keepTools" : true});
        }
        {
            var Q0;
            Q0=makeQuery(id+"F10.opExtrude","SWEPT_BODY",BODY,{"disambiguationData":[OSD([sQuery(id+"F9.wireOp",EDGE,"E39.bottom"),sQuery(id+"F9.wireOp",EDGE,"E39.top"),sQuery(id+"F9.wireOp",EDGE,"E39.left"),sQuery(id+"F9.wireOp",EDGE,"E39.right"),sQuery(id+"F9.wireOp",EDGE,"E40.bottom"),sQuery(id+"F9.wireOp",EDGE,"E40.top"),sQuery(id+"F9.wireOp",EDGE,"E40.left"),sQuery(id+"F9.wireOp",EDGE,"E40.right"),sQuery(id+"F9.wireOp",EDGE,"E41.1.0.0"),sQuery(id+"F9.wireOp",EDGE,"E41.1.0.1"),sQuery(id+"F9.wireOp",EDGE,"E41.1.0.2"),sQuery(id+"F9.wireOp",EDGE,"E41.1.0.3"),sQuery(id+"F9.wireOp",EDGE,"E41.2.0.0"),sQuery(id+"F9.wireOp",EDGE,"E41.2.0.1"),sQuery(id+"F9.wireOp",EDGE,"E41.2.0.2"),sQuery(id+"F9.wireOp",EDGE,"E41.2.0.3"),sQuery(id+"F9.wireOp",EDGE,"E41.3.0.0"),sQuery(id+"F9.wireOp",EDGE,"E41.3.0.1"),sQuery(id+"F9.wireOp",EDGE,"E41.3.0.2"),sQuery(id+"F9.wireOp",EDGE,"E41.3.0.3"),sQuery(id+"F9.wireOp",EDGE,"E41.4.0.0"),sQuery(id+"F9.wireOp",EDGE,"E41.4.0.1"),sQuery(id+"F9.wireOp",EDGE,"E41.4.0.2"),sQuery(id+"F9.wireOp",EDGE,"E41.4.0.3"),sQuery(id+"F9.wireOp",EDGE,"E41.5.0.0"),sQuery(id+"F9.wireOp",EDGE,"E41.5.0.1"),sQuery(id+"F9.wireOp",EDGE,"E41.5.0.2"),sQuery(id+"F9.wireOp",EDGE,"E41.5.0.3"),sQuery(id+"F9.wireOp",EDGE,"E41.6.0.0"),sQuery(id+"F9.wireOp",EDGE,"E41.6.0.1"),sQuery(id+"F9.wireOp",EDGE,"E41.6.0.2"),sQuery(id+"F9.wireOp",EDGE,"E41.6.0.3"),sQuery(id+"F9.wireOp",EDGE,"E41.7.0.0"),sQuery(id+"F9.wireOp",EDGE,"E41.7.0.1"),sQuery(id+"F9.wireOp",EDGE,"E41.7.0.2"),sQuery(id+"F9.wireOp",EDGE,"E41.7.0.3"),sQuery(id+"F9.wireOp",EDGE,"E41.8.0.0"),sQuery(id+"F9.wireOp",EDGE,"E41.8.0.1"),sQuery(id+"F9.wireOp",EDGE,"E41.8.0.2"),sQuery(id+"F9.wireOp",EDGE,"E41.8.0.3"),sQuery(id+"F9.wireOp",EDGE,"E41.9.0.0"),sQuery(id+"F9.wireOp",EDGE,"E41.9.0.1"),sQuery(id+"F9.wireOp",EDGE,"E41.9.0.2"),sQuery(id+"F9.wireOp",EDGE,"E41.9.0.3"),sQuery(id+"F9.wireOp",EDGE,"E95"),sQuery(id+"F9.wireOp",EDGE,"E96"),sQuery(id+"F9.wireOp",EDGE,"E100.MirrorC"),sQuery(id+"F9.wireOp",EDGE,"E101.MirrorC")])]});
            var Q1;
            Q1=sQuery(id+"F9.wireOp",EDGE,"E99");
            transform(context, id + "F13", {"entities" : qUnion([Q0]), "transformType" : TransformType.ROTATION, "transformAxis" : qUnion([Q1]), "angle" : 180 * degree, "makeCopy" : true});
        }
        {
            var Q0;
            Q0=makeQuery(id+"F13.opPattern","COPY",BODY,{"derivedFrom":makeQuery(id+"F10.opExtrude","SWEPT_BODY",BODY,{"disambiguationData":[OSD([sQuery(id+"F9.wireOp",EDGE,"E39.bottom"),sQuery(id+"F9.wireOp",EDGE,"E39.top"),sQuery(id+"F9.wireOp",EDGE,"E39.left"),sQuery(id+"F9.wireOp",EDGE,"E39.right"),sQuery(id+"F9.wireOp",EDGE,"E40.bottom"),sQuery(id+"F9.wireOp",EDGE,"E40.top"),sQuery(id+"F9.wireOp",EDGE,"E40.left"),sQuery(id+"F9.wireOp",EDGE,"E40.right"),sQuery(id+"F9.wireOp",EDGE,"E41.1.0.0"),sQuery(id+"F9.wireOp",EDGE,"E41.1.0.1"),sQuery(id+"F9.wireOp",EDGE,"E41.1.0.2"),sQuery(id+"F9.wireOp",EDGE,"E41.1.0.3"),sQuery(id+"F9.wireOp",EDGE,"E41.2.0.0"),sQuery(id+"F9.wireOp",EDGE,"E41.2.0.1"),sQuery(id+"F9.wireOp",EDGE,"E41.2.0.2"),sQuery(id+"F9.wireOp",EDGE,"E41.2.0.3"),sQuery(id+"F9.wireOp",EDGE,"E41.3.0.0"),sQuery(id+"F9.wireOp",EDGE,"E41.3.0.1"),sQuery(id+"F9.wireOp",EDGE,"E41.3.0.2"),sQuery(id+"F9.wireOp",EDGE,"E41.3.0.3"),sQuery(id+"F9.wireOp",EDGE,"E41.4.0.0"),sQuery(id+"F9.wireOp",EDGE,"E41.4.0.1"),sQuery(id+"F9.wireOp",EDGE,"E41.4.0.2"),sQuery(id+"F9.wireOp",EDGE,"E41.4.0.3"),sQuery(id+"F9.wireOp",EDGE,"E41.5.0.0"),sQuery(id+"F9.wireOp",EDGE,"E41.5.0.1"),sQuery(id+"F9.wireOp",EDGE,"E41.5.0.2"),sQuery(id+"F9.wireOp",EDGE,"E41.5.0.3"),sQuery(id+"F9.wireOp",EDGE,"E41.6.0.0"),sQuery(id+"F9.wireOp",EDGE,"E41.6.0.1"),sQuery(id+"F9.wireOp",EDGE,"E41.6.0.2"),sQuery(id+"F9.wireOp",EDGE,"E41.6.0.3"),sQuery(id+"F9.wireOp",EDGE,"E41.7.0.0"),sQuery(id+"F9.wireOp",EDGE,"E41.7.0.1"),sQuery(id+"F9.wireOp",EDGE,"E41.7.0.2"),sQuery(id+"F9.wireOp",EDGE,"E41.7.0.3"),sQuery(id+"F9.wireOp",EDGE,"E41.8.0.0"),sQuery(id+"F9.wireOp",EDGE,"E41.8.0.1"),sQuery(id+"F9.wireOp",EDGE,"E41.8.0.2"),sQuery(id+"F9.wireOp",EDGE,"E41.8.0.3"),sQuery(id+"F9.wireOp",EDGE,"E41.9.0.0"),sQuery(id+"F9.wireOp",EDGE,"E41.9.0.1"),sQuery(id+"F9.wireOp",EDGE,"E41.9.0.2"),sQuery(id+"F9.wireOp",EDGE,"E41.9.0.3"),sQuery(id+"F9.wireOp",EDGE,"E95"),sQuery(id+"F9.wireOp",EDGE,"E96"),sQuery(id+"F9.wireOp",EDGE,"E100.MirrorC"),sQuery(id+"F9.wireOp",EDGE,"E101.MirrorC")])]}),"instanceName":"1"});
            transform(context, id + "F14", {"entities" : qUnion([Q0]), "transformType" : TransformType.TRANSLATION_3D, "dx" : 0 * mm, "dy" : -(getVariable(context, 'lev')) * mm, "dz" : 0 * mm, "makeCopy" : false});
        }
        {
            var Q0;
            Q0=makeQuery(id+"F13.opPattern","COPY",FACE,{"derivedFrom":makeQuery(id+"F10.opExtrude","SWEPT_FACE",FACE,{"disambiguationData":[OSD([sQuery(id+"F9.wireOp",EDGE,"E41.9.0.0")])]}),"instanceName":"1"});
            var sketch = newSketch(context, id + "F15", { "sketchPlane" : qUnion([Q0])});
            skLineSegment(sketch, "E104.bottom", {"start": v(-1588, 500) * mm, "end": v(12, 500) * mm});
            skLineSegment(sketch, "E104.top", {"start": v(-1588, 0) * mm, "end": v(12, 0) * mm});
            skLineSegment(sketch, "E104.left", {"start": v(-1588, 500) * mm, "end": v(-1588, 0) * mm});
            skLineSegment(sketch, "E104.right", {"start": v(12, 500) * mm, "end": v(12, 0) * mm});
            skSolve(sketch);
        }
        {
            var Q0;
            Q0 = qSketchRegion(id + "F15", true);
            extrude(context, id + "F16", {"entities" : qUnion([Q0]), "depth" : (getVariable(context, 'vaneri')) * mm});
        }
        {
            var Q0;
            Q0=makeQuery(id+"F7.opPattern","COPY",BODY,{"derivedFrom":makeQuery(id+"F5.opExtrude","SWEPT_BODY",BODY,{"disambiguationData":[OSD([sQuery(id+"F4.wireOp",EDGE,"E0.bottom"),sQuery(id+"F4.wireOp",EDGE,"E0.top"),sQuery(id+"F4.wireOp",EDGE,"E0.right"),sQuery(id+"F4.wireOp",EDGE,"E1.bottom"),sQuery(id+"F4.wireOp",EDGE,"E1.top"),sQuery(id+"F4.wireOp",EDGE,"E1.right"),sQuery(id+"F4.wireOp",EDGE,"E2.trimOffspring"),sQuery(id+"F4.wireOp",EDGE,"E3"),sQuery(id+"F4.wireOp",EDGE,"E4.bottom"),sQuery(id+"F4.wireOp",EDGE,"E4.top"),sQuery(id+"F4.wireOp",EDGE,"E4.right"),sQuery(id+"F4.wireOp",EDGE,"E5.trimOffspring"),sQuery(id+"F4.wireOp",EDGE,"E6"),sQuery(id+"F4.wireOp",EDGE,"E7"),sQuery(id+"F4.wireOp",EDGE,"E9.MirrorCS"),sQuery(id+"F4.wireOp",EDGE,"E10.MirrorCS"),sQuery(id+"F4.wireOp",EDGE,"E11.MirrorCS"),sQuery(id+"F4.wireOp",EDGE,"E12.MirrorCS"),sQuery(id+"F4.wireOp",EDGE,"E13.MirrorCS"),sQuery(id+"F4.wireOp",EDGE,"E14.MirrorCS"),sQuery(id+"F4.wireOp",EDGE,"E15.MirrorC"),sQuery(id+"F4.wireOp",EDGE,"E16.MirrorC"),sQuery(id+"F4.wireOp",EDGE,"E17.MirrorC"),sQuery(id+"F4.wireOp",EDGE,"E19.MirrorCS"),sQuery(id+"F4.wireOp",EDGE,"E23.MirrorCS"),sQuery(id+"F4.wireOp",EDGE,"E24.MirrorCS"),sQuery(id+"F4.wireOp",EDGE,"E27.bottom"),sQuery(id+"F4.wireOp",EDGE,"E27.top"),sQuery(id+"F4.wireOp",EDGE,"E27.left"),sQuery(id+"F4.wireOp",EDGE,"E27.right"),sQuery(id+"F4.wireOp",EDGE,"E28.1.0.0"),sQuery(id+"F4.wireOp",EDGE,"E28.1.0.1"),sQuery(id+"F4.wireOp",EDGE,"E28.1.0.2"),sQuery(id+"F4.wireOp",EDGE,"E28.1.0.3"),sQuery(id+"F4.wireOp",EDGE,"E28.2.0.0"),sQuery(id+"F4.wireOp",EDGE,"E28.2.0.1"),sQuery(id+"F4.wireOp",EDGE,"E28.2.0.2"),sQuery(id+"F4.wireOp",EDGE,"E28.2.0.3")])]}),"instanceName":"1"});
            var Q1;
            Q1=makeQuery(id+"F10.opExtrude","SWEPT_BODY",BODY,{"disambiguationData":[OSD([sQuery(id+"F9.wireOp",EDGE,"E39.bottom"),sQuery(id+"F9.wireOp",EDGE,"E39.top"),sQuery(id+"F9.wireOp",EDGE,"E39.left"),sQuery(id+"F9.wireOp",EDGE,"E39.right"),sQuery(id+"F9.wireOp",EDGE,"E40.bottom"),sQuery(id+"F9.wireOp",EDGE,"E40.top"),sQuery(id+"F9.wireOp",EDGE,"E40.left"),sQuery(id+"F9.wireOp",EDGE,"E40.right"),sQuery(id+"F9.wireOp",EDGE,"E41.1.0.0"),sQuery(id+"F9.wireOp",EDGE,"E41.1.0.1"),sQuery(id+"F9.wireOp",EDGE,"E41.1.0.2"),sQuery(id+"F9.wireOp",EDGE,"E41.1.0.3"),sQuery(id+"F9.wireOp",EDGE,"E41.2.0.0"),sQuery(id+"F9.wireOp",EDGE,"E41.2.0.1"),sQuery(id+"F9.wireOp",EDGE,"E41.2.0.2"),sQuery(id+"F9.wireOp",EDGE,"E41.2.0.3"),sQuery(id+"F9.wireOp",EDGE,"E41.3.0.0"),sQuery(id+"F9.wireOp",EDGE,"E41.3.0.1"),sQuery(id+"F9.wireOp",EDGE,"E41.3.0.2"),sQuery(id+"F9.wireOp",EDGE,"E41.3.0.3"),sQuery(id+"F9.wireOp",EDGE,"E41.4.0.0"),sQuery(id+"F9.wireOp",EDGE,"E41.4.0.1"),sQuery(id+"F9.wireOp",EDGE,"E41.4.0.2"),sQuery(id+"F9.wireOp",EDGE,"E41.4.0.3"),sQuery(id+"F9.wireOp",EDGE,"E41.5.0.0"),sQuery(id+"F9.wireOp",EDGE,"E41.5.0.1"),sQuery(id+"F9.wireOp",EDGE,"E41.5.0.2"),sQuery(id+"F9.wireOp",EDGE,"E41.5.0.3"),sQuery(id+"F9.wireOp",EDGE,"E41.6.0.0"),sQuery(id+"F9.wireOp",EDGE,"E41.6.0.1"),sQuery(id+"F9.wireOp",EDGE,"E41.6.0.2"),sQuery(id+"F9.wireOp",EDGE,"E41.6.0.3"),sQuery(id+"F9.wireOp",EDGE,"E41.7.0.0"),sQuery(id+"F9.wireOp",EDGE,"E41.7.0.1"),sQuery(id+"F9.wireOp",EDGE,"E41.7.0.2"),sQuery(id+"F9.wireOp",EDGE,"E41.7.0.3"),sQuery(id+"F9.wireOp",EDGE,"E41.8.0.0"),sQuery(id+"F9.wireOp",EDGE,"E41.8.0.1"),sQuery(id+"F9.wireOp",EDGE,"E41.8.0.2"),sQuery(id+"F9.wireOp",EDGE,"E41.8.0.3"),sQuery(id+"F9.wireOp",EDGE,"E41.9.0.0"),sQuery(id+"F9.wireOp",EDGE,"E41.9.0.1"),sQuery(id+"F9.wireOp",EDGE,"E41.9.0.2"),sQuery(id+"F9.wireOp",EDGE,"E41.9.0.3"),sQuery(id+"F9.wireOp",EDGE,"E95"),sQuery(id+"F9.wireOp",EDGE,"E96"),sQuery(id+"F9.wireOp",EDGE,"E100.MirrorC"),sQuery(id+"F9.wireOp",EDGE,"E101.MirrorC")])]});
            var Q2;
            Q2=makeQuery(id+"F13.opPattern","COPY",BODY,{"derivedFrom":makeQuery(id+"F10.opExtrude","SWEPT_BODY",BODY,{"disambiguationData":[OSD([sQuery(id+"F9.wireOp",EDGE,"E39.bottom"),sQuery(id+"F9.wireOp",EDGE,"E39.top"),sQuery(id+"F9.wireOp",EDGE,"E39.left"),sQuery(id+"F9.wireOp",EDGE,"E39.right"),sQuery(id+"F9.wireOp",EDGE,"E40.bottom"),sQuery(id+"F9.wireOp",EDGE,"E40.top"),sQuery(id+"F9.wireOp",EDGE,"E40.left"),sQuery(id+"F9.wireOp",EDGE,"E40.right"),sQuery(id+"F9.wireOp",EDGE,"E41.1.0.0"),sQuery(id+"F9.wireOp",EDGE,"E41.1.0.1"),sQuery(id+"F9.wireOp",EDGE,"E41.1.0.2"),sQuery(id+"F9.wireOp",EDGE,"E41.1.0.3"),sQuery(id+"F9.wireOp",EDGE,"E41.2.0.0"),sQuery(id+"F9.wireOp",EDGE,"E41.2.0.1"),sQuery(id+"F9.wireOp",EDGE,"E41.2.0.2"),sQuery(id+"F9.wireOp",EDGE,"E41.2.0.3"),sQuery(id+"F9.wireOp",EDGE,"E41.3.0.0"),sQuery(id+"F9.wireOp",EDGE,"E41.3.0.1"),sQuery(id+"F9.wireOp",EDGE,"E41.3.0.2"),sQuery(id+"F9.wireOp",EDGE,"E41.3.0.3"),sQuery(id+"F9.wireOp",EDGE,"E41.4.0.0"),sQuery(id+"F9.wireOp",EDGE,"E41.4.0.1"),sQuery(id+"F9.wireOp",EDGE,"E41.4.0.2"),sQuery(id+"F9.wireOp",EDGE,"E41.4.0.3"),sQuery(id+"F9.wireOp",EDGE,"E41.5.0.0"),sQuery(id+"F9.wireOp",EDGE,"E41.5.0.1"),sQuery(id+"F9.wireOp",EDGE,"E41.5.0.2"),sQuery(id+"F9.wireOp",EDGE,"E41.5.0.3"),sQuery(id+"F9.wireOp",EDGE,"E41.6.0.0"),sQuery(id+"F9.wireOp",EDGE,"E41.6.0.1"),sQuery(id+"F9.wireOp",EDGE,"E41.6.0.2"),sQuery(id+"F9.wireOp",EDGE,"E41.6.0.3"),sQuery(id+"F9.wireOp",EDGE,"E41.7.0.0"),sQuery(id+"F9.wireOp",EDGE,"E41.7.0.1"),sQuery(id+"F9.wireOp",EDGE,"E41.7.0.2"),sQuery(id+"F9.wireOp",EDGE,"E41.7.0.3"),sQuery(id+"F9.wireOp",EDGE,"E41.8.0.0"),sQuery(id+"F9.wireOp",EDGE,"E41.8.0.1"),sQuery(id+"F9.wireOp",EDGE,"E41.8.0.2"),sQuery(id+"F9.wireOp",EDGE,"E41.8.0.3"),sQuery(id+"F9.wireOp",EDGE,"E41.9.0.0"),sQuery(id+"F9.wireOp",EDGE,"E41.9.0.1"),sQuery(id+"F9.wireOp",EDGE,"E41.9.0.2"),sQuery(id+"F9.wireOp",EDGE,"E41.9.0.3"),sQuery(id+"F9.wireOp",EDGE,"E95"),sQuery(id+"F9.wireOp",EDGE,"E96"),sQuery(id+"F9.wireOp",EDGE,"E100.MirrorC"),sQuery(id+"F9.wireOp",EDGE,"E101.MirrorC")])]}),"instanceName":"1"});
            var Q3;
            Q3=makeQuery(id+"F5.opExtrude","SWEPT_BODY",BODY,{"disambiguationData":[OSD([sQuery(id+"F4.wireOp",EDGE,"E0.bottom"),sQuery(id+"F4.wireOp",EDGE,"E0.top"),sQuery(id+"F4.wireOp",EDGE,"E0.right"),sQuery(id+"F4.wireOp",EDGE,"E1.bottom"),sQuery(id+"F4.wireOp",EDGE,"E1.top"),sQuery(id+"F4.wireOp",EDGE,"E1.right"),sQuery(id+"F4.wireOp",EDGE,"E2.trimOffspring"),sQuery(id+"F4.wireOp",EDGE,"E3"),sQuery(id+"F4.wireOp",EDGE,"E4.bottom"),sQuery(id+"F4.wireOp",EDGE,"E4.top"),sQuery(id+"F4.wireOp",EDGE,"E4.right"),sQuery(id+"F4.wireOp",EDGE,"E5.trimOffspring"),sQuery(id+"F4.wireOp",EDGE,"E6"),sQuery(id+"F4.wireOp",EDGE,"E7"),sQuery(id+"F4.wireOp",EDGE,"E9.MirrorCS"),sQuery(id+"F4.wireOp",EDGE,"E10.MirrorCS"),sQuery(id+"F4.wireOp",EDGE,"E11.MirrorCS"),sQuery(id+"F4.wireOp",EDGE,"E12.MirrorCS"),sQuery(id+"F4.wireOp",EDGE,"E13.MirrorCS"),sQuery(id+"F4.wireOp",EDGE,"E14.MirrorCS"),sQuery(id+"F4.wireOp",EDGE,"E15.MirrorC"),sQuery(id+"F4.wireOp",EDGE,"E16.MirrorC"),sQuery(id+"F4.wireOp",EDGE,"E17.MirrorC"),sQuery(id+"F4.wireOp",EDGE,"E19.MirrorCS"),sQuery(id+"F4.wireOp",EDGE,"E23.MirrorCS"),sQuery(id+"F4.wireOp",EDGE,"E24.MirrorCS"),sQuery(id+"F4.wireOp",EDGE,"E27.bottom"),sQuery(id+"F4.wireOp",EDGE,"E27.top"),sQuery(id+"F4.wireOp",EDGE,"E27.left"),sQuery(id+"F4.wireOp",EDGE,"E27.right"),sQuery(id+"F4.wireOp",EDGE,"E28.1.0.0"),sQuery(id+"F4.wireOp",EDGE,"E28.1.0.1"),sQuery(id+"F4.wireOp",EDGE,"E28.1.0.2"),sQuery(id+"F4.wireOp",EDGE,"E28.1.0.3"),sQuery(id+"F4.wireOp",EDGE,"E28.2.0.0"),sQuery(id+"F4.wireOp",EDGE,"E28.2.0.1"),sQuery(id+"F4.wireOp",EDGE,"E28.2.0.2"),sQuery(id+"F4.wireOp",EDGE,"E28.2.0.3")])]});
            var Q4;
            Q4=makeQuery(id+"F16.opExtrude","SWEPT_BODY",BODY,{"disambiguationData":[OSD([sQuery(id+"F15.wireOp",EDGE,"E104.bottom"),sQuery(id+"F15.wireOp",EDGE,"E104.top"),sQuery(id+"F15.wireOp",EDGE,"E104.left"),sQuery(id+"F15.wireOp",EDGE,"E104.right")])]});
            booleanBodies(context, id + "F17", {"operationType" : BooleanOperationType.SUBTRACTION, "tools" : qUnion([Q0, Q1, Q2, Q3]), "targets" : qUnion([Q4]), "keepTools" : true});
        }
    });
